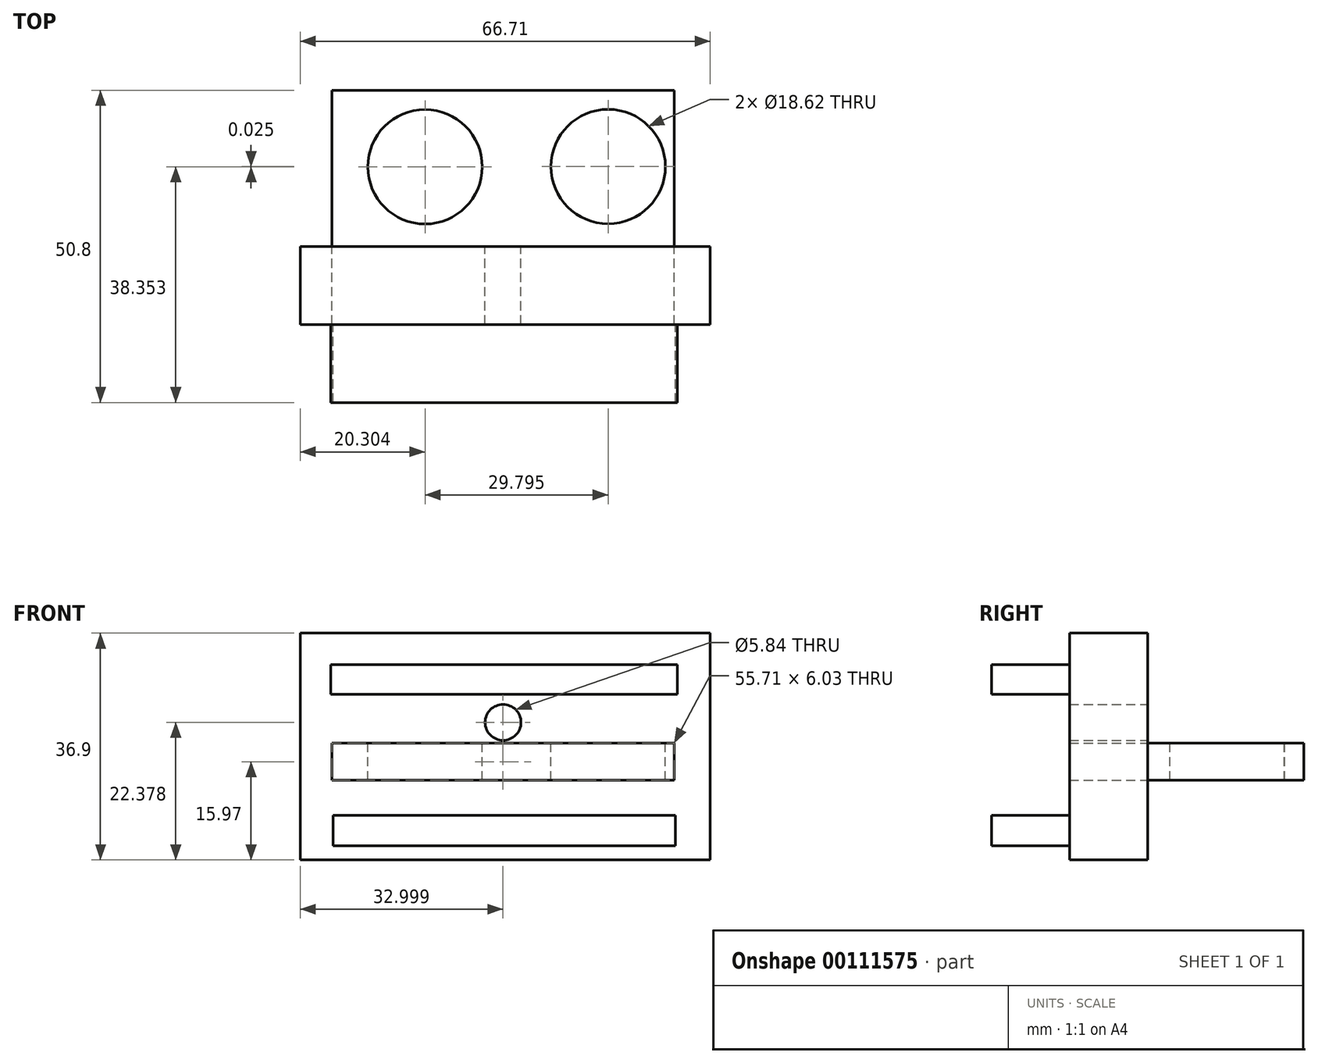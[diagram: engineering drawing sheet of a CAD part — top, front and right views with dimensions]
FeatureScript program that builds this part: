
annotation { "Feature Type Name" : "Feature", "Feature Type Description" : "" }
export const myFeature = defineFeature(function(context is Context, id is Id, definition is map)
    precondition{}
    {
        {
            var Q0;
            Q0=qCreatedBy(makeId("Front.planeOp"),FACE);
            var sketch = newSketch(context, id + "F0", { "sketchPlane" : qUnion([Q0])});
            skLineSegment(sketch, "E0", {"start": v(-31.58, 20.93) * mm, "end": v(-31.58, -15.97) * mm});
            skLineSegment(sketch, "E1", {"start": v(-31.58, 20.93) * mm, "end": v(35.13, 20.93) * mm});
            skLineSegment(sketch, "E2", {"start": v(35.13, 20.93) * mm, "end": v(35.13, -15.97) * mm});
            skLineSegment(sketch, "E3", {"start": v(-31.58, -15.97) * mm, "end": v(35.13, -15.97) * mm});
            skLineSegment(sketch, "E4", {"start": v(-26.61, 15.79) * mm, "end": v(29.8, 15.79) * mm});
            skLineSegment(sketch, "E5", {"start": v(29.8, 15.79) * mm, "end": v(29.8, 11) * mm});
            skLineSegment(sketch, "E6", {"start": v(29.8, 11) * mm, "end": v(-26.61, 11) * mm});
            skLineSegment(sketch, "E7", {"start": v(-26.61, 11) * mm, "end": v(-26.61, 15.79) * mm});
            skLineSegment(sketch, "E8", {"start": v(-26.43, 3.02) * mm, "end": v(29.27, 3.02) * mm});
            skLineSegment(sketch, "E9", {"start": v(29.27, 3.02) * mm, "end": v(29.27, -3.02) * mm});
            skLineSegment(sketch, "E10", {"start": v(29.27, -3.02) * mm, "end": v(-26.43, -3.02) * mm});
            skLineSegment(sketch, "E11", {"start": v(-26.43, -3.02) * mm, "end": v(-26.43, 3.02) * mm});
            skLineSegment(sketch, "E12", {"start": v(-26.26, -8.7) * mm, "end": v(29.45, -8.7) * mm});
            skLineSegment(sketch, "E13", {"start": v(29.45, -8.7) * mm, "end": v(29.45, -13.66) * mm});
            skLineSegment(sketch, "E14", {"start": v(29.45, -13.66) * mm, "end": v(-26.26, -13.66) * mm});
            skLineSegment(sketch, "E15", {"start": v(-26.26, -13.66) * mm, "end": v(-26.26, -8.7) * mm});
            skCircle(sketch, "E16", {"center": v(1.42, 6.4) * mm, "radius": 2.92 * mm});
            skPoint(sketch, "E16.centerSnap0", {"position": v(1.42, 3.02) * mm});
            skSolve(sketch);
        }
        {
            var Q0;
            Q0=makeQuery(id+"F0.imprint","IMPRINT",FACE,{"disambiguationData":[TD([[makeQuery(id+"F0.imprint","IMPRINT",EDGE,{"derivedFrom":sQuery(id+"F0.wireOp",EDGE,"E0")}),1.0]])]});
            extrude(context, id + "F1", {"entities" : qUnion([Q0]), "depth" : 12.7 * mm});
        }
        {
            var Q0;
            Q0=makeQuery(id+"F0.imprint","IMPRINT",FACE,{"disambiguationData":[TD([[makeQuery(id+"F0.imprint","IMPRINT",EDGE,{"derivedFrom":sQuery(id+"F0.wireOp",EDGE,"E4")}),-1.0]])]});
            var Q1;
            Q1=makeQuery(id+"F0.imprint","IMPRINT",FACE,{"disambiguationData":[TD([[makeQuery(id+"F0.imprint","IMPRINT",EDGE,{"derivedFrom":sQuery(id+"F0.wireOp",EDGE,"E12")}),-1.0]])]});
            extrude(context, id + "F2", {"entities" : qUnion([Q0, Q1]), "operationType" : NewBodyOperationType.ADD, "depth" : 25.4 * mm});
        }
        {
            var Q0;
            Q0=makeQuery(id+"F0.imprint","IMPRINT",FACE,{"disambiguationData":[TD([[makeQuery(id+"F0.imprint","IMPRINT",EDGE,{"derivedFrom":sQuery(id+"F0.wireOp",EDGE,"E8")}),-1.0]])]});
            extrude(context, id + "F3", {"entities" : qUnion([Q0]), "oppositeDirection" : true, "depth" : 25.4 * mm});
        }
        {
            var Q0;
            Q0=makeQuery(id+"F3.opExtrude","SWEPT_FACE",FACE,{"disambiguationData":[OSD([sQuery(id+"F0.wireOp",EDGE,"E8")])]});
            var sketch = newSketch(context, id + "F4", { "sketchPlane" : qUnion([Q0])});
            skCircle(sketch, "E17", {"center": v(18.52, 12.98) * mm, "radius": 9.3 * mm});
            skCircle(sketch, "E18", {"center": v(-11.28, 12.95) * mm, "radius": 9.3 * mm});
            skSolve(sketch);
        }
        {
            var Q0;
            Q0=makeQuery(id+"F4.imprint","IMPRINT",FACE,{"disambiguationData":[TD([[makeQuery(id+"F4.imprint","IMPRINT",EDGE,{"derivedFrom":sQuery(id+"F4.wireOp",EDGE,"E17")}),1.0]])]});
            var Q1;
            Q1=makeQuery(id+"F4.imprint","IMPRINT",FACE,{"disambiguationData":[TD([[makeQuery(id+"F4.imprint","IMPRINT",EDGE,{"derivedFrom":sQuery(id+"F4.wireOp",EDGE,"E18")}),1.0]])]});
            extrude(context, id + "F5", {"entities" : qUnion([Q0, Q1]), "operationType" : NewBodyOperationType.REMOVE, "oppositeDirection" : true, "depth" : 25.4 * mm});
        }
        {
            var Q0;
            Q0=makeQuery(id+"F0.imprint","IMPRINT",FACE,{"disambiguationData":[TD([[makeQuery(id+"F0.imprint","IMPRINT",EDGE,{"derivedFrom":sQuery(id+"F0.wireOp",EDGE,"E16")}),1.0]])]});
            extrude(context, id + "F6", {"entities" : qUnion([Q0]), "operationType" : NewBodyOperationType.REMOVE, "oppositeDirection" : true, "depth" : 7.13 * mm});
        }
    });
